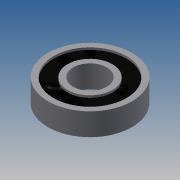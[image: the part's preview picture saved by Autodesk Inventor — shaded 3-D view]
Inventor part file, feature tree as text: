
AUTODESK INVENTOR PART (.ipt)
format: ipt  version: 2017 (Build 210142000, 142)  size: 161,280 bytes
history: native  units: mm
features: other x1, revolve x1, sketch x1
ambient origin geometry x8: Origin, YZ Plane, XZ Plane, XY Plane, X Axis, Y Axis, Z Axis, Center Point
bodies: Body1 (feature_tree)
feature tree (3):
  other  "Sólido1"
  revolve  "Revolución1"  [1 undecoded]
  sketch  "Boceto1"  dims[d0=1.0mm d1=0.3mm d2=30.0mm d3=8.0mm d4=0.8mm d5=2.0mm d6=12.0mm d7=90.0deg]
note: 1 required parameter value undecoded (feature->parameter linkage not recoverable at this tier; creation-order binding heuristic only, values carry confidence <= 0.55)
